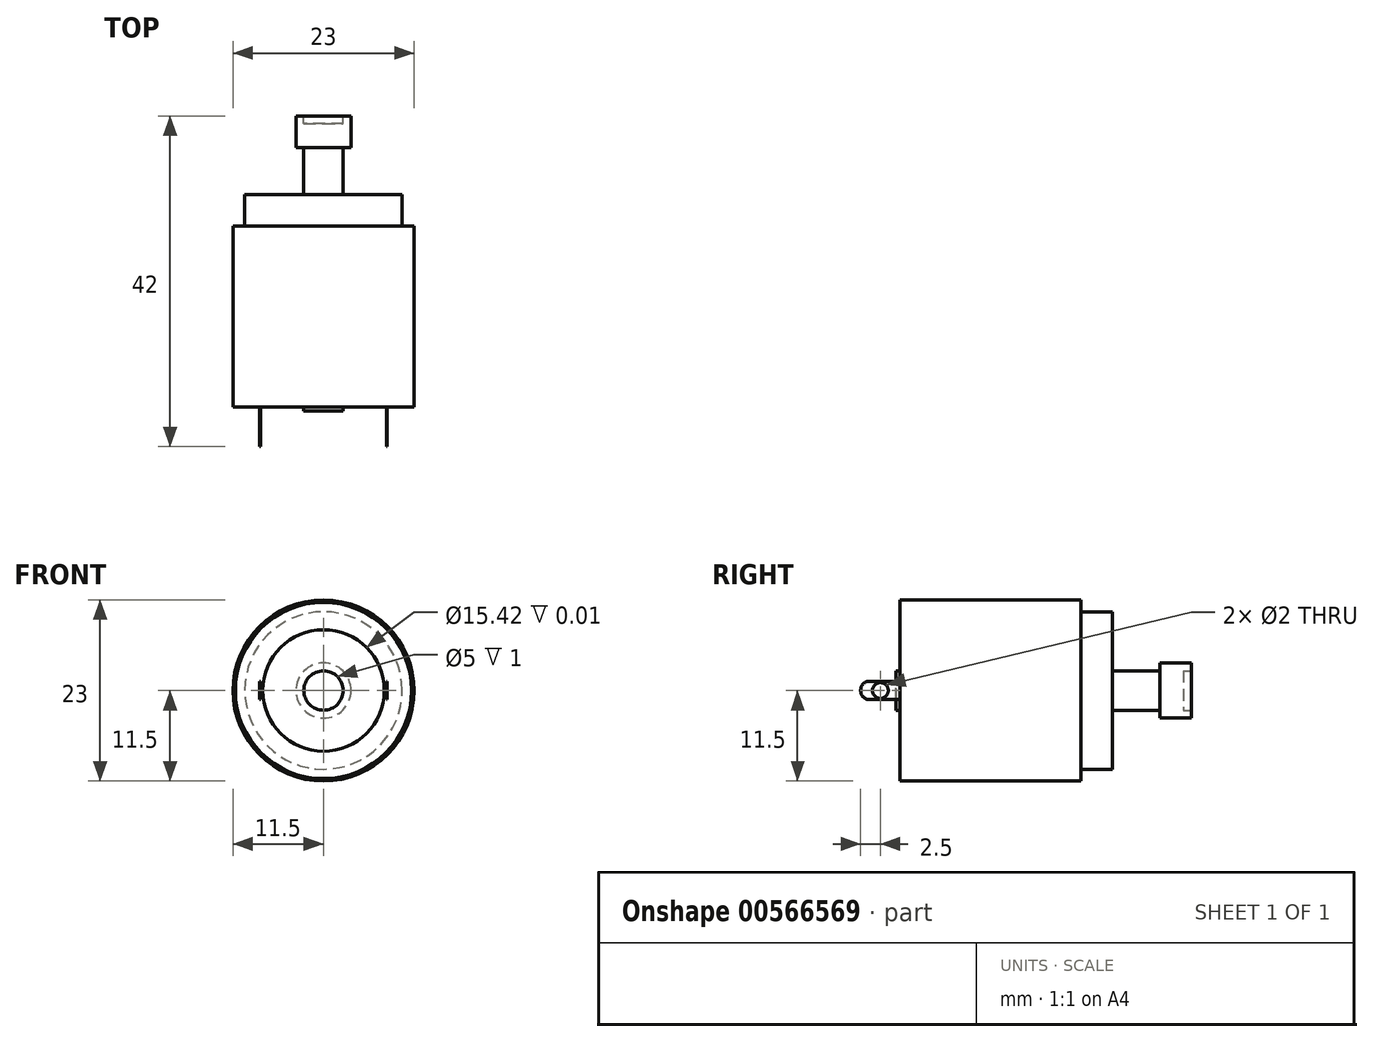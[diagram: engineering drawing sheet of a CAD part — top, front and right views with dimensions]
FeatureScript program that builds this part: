
annotation { "Feature Type Name" : "Feature", "Feature Type Description" : "" }
export const myFeature = defineFeature(function(context is Context, id is Id, definition is map)
    precondition{}
    {
        {
            var Q0;
            Q0=qCreatedBy(makeId("Front.planeOp"),FACE);
            var sketch = newSketch(context, id + "F0", { "sketchPlane" : qUnion([Q0])});
            skCircle(sketch, "E0", {"center": v(0, 0) * mm, "radius": 11.5 * mm});
            skSolve(sketch);
        }
        {
            var Q0;
            Q0 = qSketchRegion(id + "F0", true);
            extrude(context, id + "F1", {"entities" : qUnion([Q0]), "depth" : 23 * mm, "offsetDistance" : 25 * mm});
        }
        {
            var Q0;
            Q0=makeQuery(id+"F1.opExtrude","CAP_FACE",FACE,{"disambiguationData":[OSD([sQuery(id+"F0.wireOp",EDGE,"E0")])],"isStart":true});
            var sketch = newSketch(context, id + "F2", { "sketchPlane" : qUnion([Q0])});
            skCircle(sketch, "E1", {"center": v(0, 0) * mm, "radius": 10 * mm});
            skSolve(sketch);
        }
        {
            var Q0;
            Q0 = qSketchRegion(id + "F2", true);
            extrude(context, id + "F3", {"entities" : qUnion([Q0]), "operationType" : NewBodyOperationType.ADD, "depth" : 4 * mm, "offsetDistance" : 25 * mm});
        }
        {
            var Q0;
            Q0=makeQuery(id+"F1.opExtrude","CAP_FACE",FACE,{"disambiguationData":[OSD([sQuery(id+"F0.wireOp",EDGE,"E0")])],"isStart":false});
            var sketch = newSketch(context, id + "F4", { "sketchPlane" : qUnion([Q0])});
            skLineSegment(sketch, "E2", {"start": v(0, 16.99) * mm, "end": v(0, -14.83) * mm, "construction": true});
            skLineSegment(sketch, "E3.bottom", {"start": v(-8.1, 1.18) * mm, "end": v(-8, 1.18) * mm});
            skLineSegment(sketch, "E3.top", {"start": v(-8.1, -1.15) * mm, "end": v(-8, -1.15) * mm});
            skLineSegment(sketch, "E3.left", {"start": v(-8.1, 1.18) * mm, "end": v(-8.1, -1.15) * mm});
            skLineSegment(sketch, "E3.right", {"start": v(-8, 1.18) * mm, "end": v(-8, -1.15) * mm});
            skLineSegment(sketch, "E4", {"start": v(-8, 0) * mm, "end": v(0, 0.02) * mm, "construction": true});
            skPoint(sketch, "E4.endSnap0", {"position": v(-8, 0.02) * mm});
            skSolve(sketch);
        }
        {
            var Q0;
            Q0 = qSketchRegion(id + "F4", true);
            extrude(context, id + "F5", {"entities" : qUnion([Q0]), "operationType" : NewBodyOperationType.ADD, "depth" : 5 * mm, "offsetDistance" : 25 * mm});
        }
        {
            var Q0;
            Q0=makeQuery(id+"F5.opExtrude","SWEPT_FACE",FACE,{"disambiguationData":[OSD([sQuery(id+"F4.wireOp",EDGE,"E3.right")])]});
            var sketch = newSketch(context, id + "F6", { "sketchPlane" : qUnion([Q0])});
            skCircle(sketch, "E5", {"center": v(-25.5, 0) * mm, "radius": 1 * mm});
            skPoint(sketch, "E5.centerSnap0", {"position": v(-25.5, 1.18) * mm});
            skLineSegment(sketch, "E6", {"start": v(-24.5, 0) * mm, "end": v(-23, 0) * mm, "construction": true});
            skSolve(sketch);
        }
        {
            var Q0;
            Q0 = qSketchRegion(id + "F6", true);
            extrude(context, id + "F7", {"entities" : qUnion([Q0]), "operationType" : NewBodyOperationType.REMOVE, "oppositeDirection" : true, "depth" : 25 * mm, "offsetDistance" : 25 * mm});
        }
        {
            var Q0;
            Q0=makeQuery(id+"F5.opExtrude","CAP_EDGE",EDGE,{"disambiguationData":[OSD([sQuery(id+"F4.wireOp",EDGE,"E3.top")])],"isStart":false});
            var Q1;
            Q1=makeQuery(id+"F5.opExtrude","CAP_EDGE",EDGE,{"disambiguationData":[OSD([sQuery(id+"F4.wireOp",EDGE,"E3.bottom")])],"isStart":false});
            fillet(context, id + "F8", {"entities" : qUnion([Q0, Q1]), "radius" : 1.1 * mm, "tangentPropagation" : true, "allowEdgeOverflow" : false});
        }
        {
            var Q0;
            Q0=makeQuery(id+"F1.opExtrude","SWEPT_BODY",BODY,{"disambiguationData":[OSD([sQuery(id+"F0.wireOp",EDGE,"E0")])]});
            var Q1;
            Q1=qCreatedBy(makeId("Right.planeOp"),FACE);
            mirror(context, id + "F9", {"operationType" : NewBodyOperationType.ADD, "entities" : qUnion([Q0]), "mirrorPlane" : qUnion([Q1])});
        }
        {
            var Q0;
            Q0=makeQuery(id+"F1.opExtrude","CAP_FACE",FACE,{"disambiguationData":[OSD([sQuery(id+"F0.wireOp",EDGE,"E0")])],"isStart":false});
            var sketch = newSketch(context, id + "F10", { "sketchPlane" : qUnion([Q0])});
            skCircle(sketch, "E7", {"center": v(0, 0) * mm, "radius": 2.5 * mm});
            skSolve(sketch);
        }
        {
            var Q0;
            Q0 = qSketchRegion(id + "F10", true);
            extrude(context, id + "F11", {"entities" : qUnion([Q0]), "operationType" : NewBodyOperationType.ADD, "oppositeDirection" : true, "depth" : 33 * mm, "offsetDistance" : 25 * mm});
        }
        {
            var Q0;
            Q0=makeQuery(id+"F1.opExtrude","CAP_FACE",FACE,{"disambiguationData":[OSD([sQuery(id+"F0.wireOp",EDGE,"E0")])],"isStart":false});
            var sketch = newSketch(context, id + "F12", { "sketchPlane" : qUnion([Q0])});
            skCircle(sketch, "E8", {"center": v(0, 0) * mm, "radius": 7.71 * mm});
            skCircle(sketch, "E9", {"center": v(0, 0) * mm, "radius": 11.2 * mm});
            skSolve(sketch);
        }
        {
            var Q0;
            Q0 = qSketchRegion(id + "F12", true);
            extrude(context, id + "F13", {"entities" : qUnion([Q0]), "operationType" : NewBodyOperationType.ADD, "depth" : 0.01 * mm, "offsetDistance" : 25 * mm});
        }
        {
            var Q0;
            Q0=makeQuery(id+"F13.boolean.opBoolean","SPLIT",FACE,{"disambiguationData":[TD([makeQuery(id+"F13.opExtrude","SWEPT_FACE",FACE,{"disambiguationData":[OSD([sQuery(id+"F12.wireOp",EDGE,"E8")])]})])],"derivedFrom":makeQuery(id+"F1.opExtrude","CAP_FACE",FACE,{"disambiguationData":[OSD([sQuery(id+"F0.wireOp",EDGE,"E0")])],"isStart":false})});
            var sketch = newSketch(context, id + "F14", { "sketchPlane" : qUnion([Q0])});
            skCircle(sketch, "E10", {"center": v(0, 0) * mm, "radius": 2.5 * mm});
            skSolve(sketch);
        }
        {
            var Q0;
            Q0 = qSketchRegion(id + "F14", true);
            extrude(context, id + "F15", {"entities" : qUnion([Q0]), "operationType" : NewBodyOperationType.ADD, "depth" : 0.5 * mm, "offsetDistance" : 25 * mm});
        }
        {
            var Q0;
            Q0=makeQuery(id+"F11.opExtrude","CAP_FACE",FACE,{"disambiguationData":[OSD([sQuery(id+"F10.wireOp",EDGE,"E7")])],"isStart":false});
            var sketch = newSketch(context, id + "F16", { "sketchPlane" : qUnion([Q0])});
            skCircle(sketch, "E11", {"center": v(0, 0) * mm, "radius": 3.5 * mm});
            skSolve(sketch);
        }
        {
            var Q0;
            Q0 = qSketchRegion(id + "F16", true);
            extrude(context, id + "F17", {"entities" : qUnion([Q0]), "operationType" : NewBodyOperationType.ADD, "depth" : 4 * mm, "offsetDistance" : 25 * mm});
        }
        {
            var Q0;
            Q0=makeQuery(id+"F17.opExtrude","CAP_FACE",FACE,{"disambiguationData":[OSD([sQuery(id+"F16.wireOp",EDGE,"E11")])],"isStart":false});
            var sketch = newSketch(context, id + "F18", { "sketchPlane" : qUnion([Q0])});
            skCircle(sketch, "E12", {"center": v(0, 0) * mm, "radius": 2.5 * mm});
            skSolve(sketch);
        }
        {
            var Q0;
            Q0 = qSketchRegion(id + "F18", true);
            extrude(context, id + "F19", {"entities" : qUnion([Q0]), "operationType" : NewBodyOperationType.REMOVE, "oppositeDirection" : true, "depth" : 1 * mm, "offsetDistance" : 25 * mm});
        }
    });
